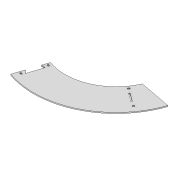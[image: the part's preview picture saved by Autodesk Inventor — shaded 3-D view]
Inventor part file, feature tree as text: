
AUTODESK INVENTOR PART (.ipt)
format: ipt  version: 2020 (Build 240168000, 168)  size: 292,864 bytes
history: native  units: mm
features: extrude x1, sketch x1
ambient origin geometry x8: Origin, YZ Plane, XZ Plane, XY Plane, X Axis, Y Axis, Z Axis, Center Point
bodies: Solid1 (feature_tree)
feature tree (2):
  extrude  "Extrusion1"  Depth=1.75mm
  sketch  "Sketch1"  dims[d0=504.787567mm d1=944.787567mm d34=1152.87mm d45=7.5mm d48=712.87mm d52=7.0mm d53=0.0mm d58=50.0mm d60=360.0deg d62=13.601997mm d63=25.0mm d65=50.0mm d71=50.0mm d72=7.5mm d74=3.5mm d75=3.5mm d79=0.0mm d80=8.0mm d81=1.75mm d83=50.0mm d84=8.0mm d85=1.75mm d86=50.0mm d88=360.0deg]
